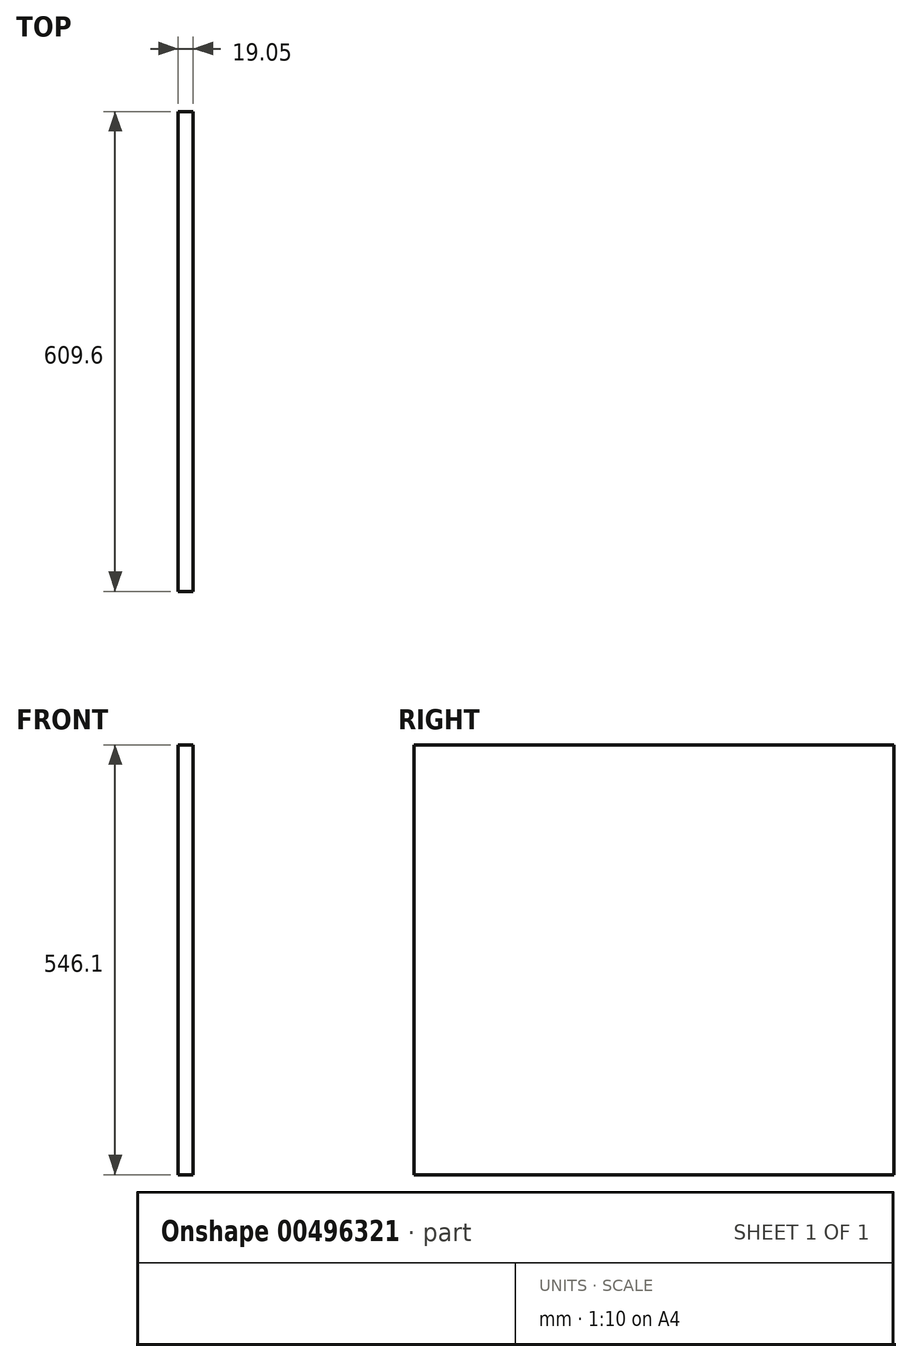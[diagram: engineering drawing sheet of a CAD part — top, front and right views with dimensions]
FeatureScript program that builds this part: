
annotation { "Feature Type Name" : "Feature", "Feature Type Description" : "" }
export const myFeature = defineFeature(function(context is Context, id is Id, definition is map)
    precondition{}
    {
        {
            var Q0;
            Q0=qCreatedBy(makeId("Right.planeOp"),FACE);
            var sketch = newSketch(context, id + "F0", { "sketchPlane" : qUnion([Q0])});
            skLineSegment(sketch, "E0.bottom", {"start": v(304.8, -273.05) * mm, "end": v(-304.8, -273.05) * mm});
            skLineSegment(sketch, "E0.top", {"start": v(304.8, 273.05) * mm, "end": v(-304.8, 273.05) * mm});
            skLineSegment(sketch, "E0.left", {"start": v(304.8, -273.05) * mm, "end": v(304.8, 273.05) * mm});
            skLineSegment(sketch, "E0.right", {"start": v(-304.8, -273.05) * mm, "end": v(-304.8, 273.05) * mm});
            skPoint(sketch, "E0.middle", {"position": v(0, 0) * mm});
            skSolve(sketch);
        }
        {
            var Q0;
            Q0 = qSketchRegion(id + "F0", true);
            extrude(context, id + "F1", {"entities" : qUnion([Q0]), "depth" : 19.05 * mm, "offsetDistance" : 25.4 * mm});
        }
    });
